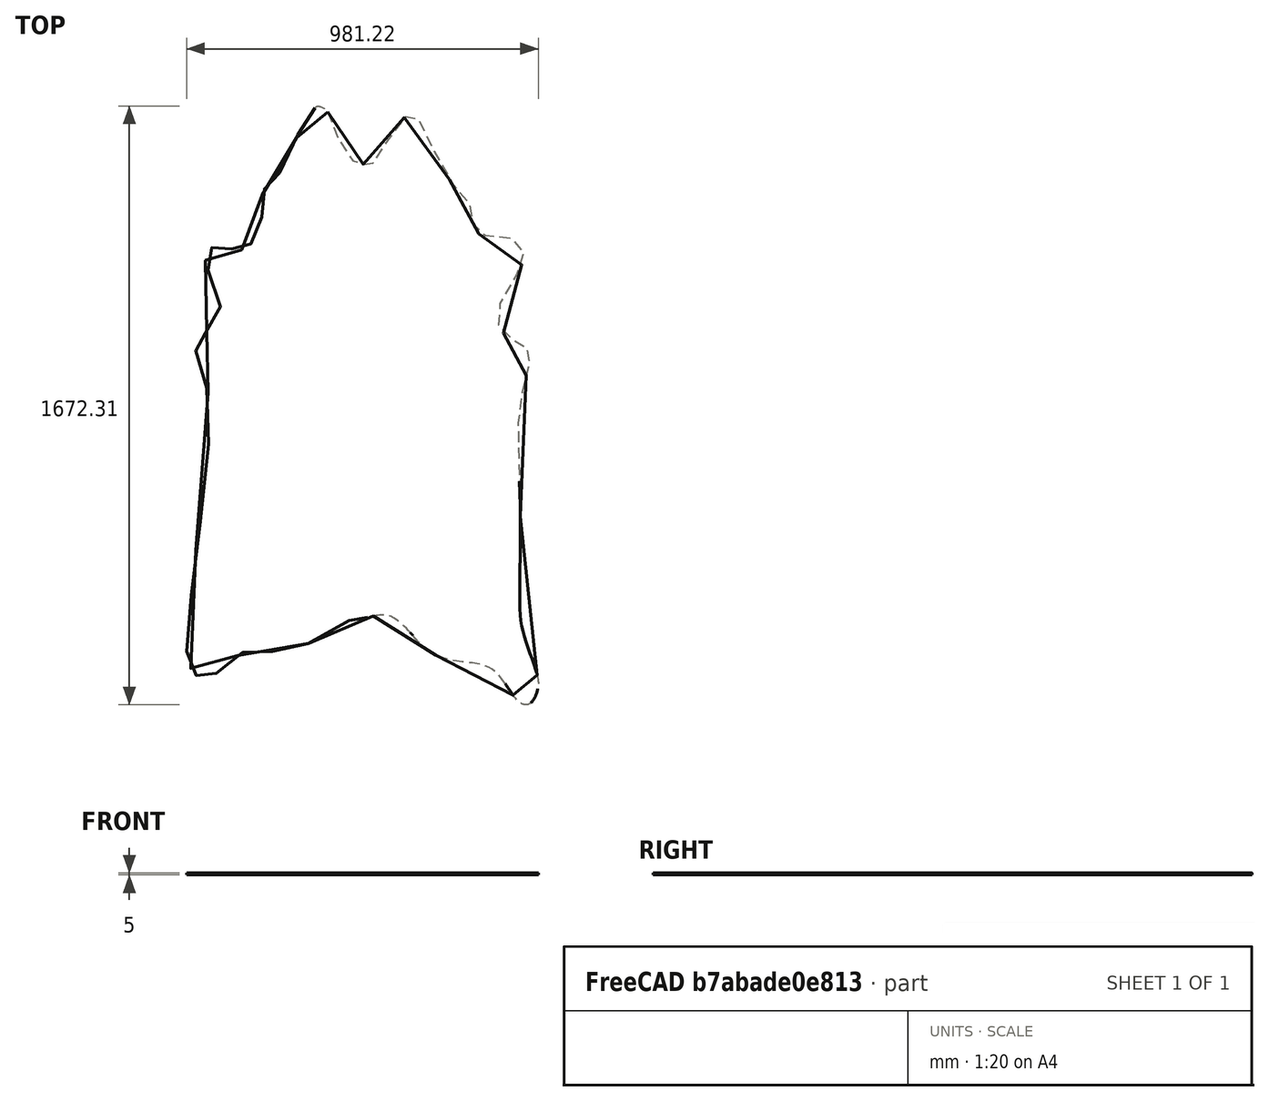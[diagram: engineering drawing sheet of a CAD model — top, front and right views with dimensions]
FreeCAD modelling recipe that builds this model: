
FCSTD DOCUMENT  (FreeCAD 0.21R33668 +26 (Git))
Label: Carpete de couro de vaca
License: All rights reserved
objects: Image::ImagePlane×2, Sketcher::SketchObject×1, Part::Extrusion×1, App::DocumentObjectGroup×1
note: 2 computed .brp shape members not serialized (recipe doc carries the construction recipe); baked Part::Feature solids carry a one-line shape summary decoded from their .brp

FEATURE [Image::ImagePlane] couro_vaca001  label="couro vaca001"
  XSize = 1300
  YSize = 1800
FEATURE [Sketcher::SketchObject] Sketch
  FullyConstrained = false
  sketch-geometry (228):
    g0-g112: Circle x113 (B-spline internal-alignment scaffolding for g113; pole/knot coordinates omitted)
    g113: BSplineCurve PolesCount=113 KnotsCount=114 Degree=3 IsPeriodic=1
    g114-g227: GeomPoint x114 (B-spline internal-alignment scaffolding for g113; pole/knot coordinates omitted)
  constraints (9):
    c: Weight(g0) = 1
    c: Equal(g0, g1-g6) x6
    c: PointOnObject(g6,g-2)
    c: Equal(g0, g7-g61) x55
    c: PointOnObject(g61,g-2)
    c: Equal(g0, g62-g112) x51
    c: PointOnObject(g112,g0)
    c: InternalAlignment(g0-g112 -> g113) x113
    c: InternalAlignment(g114-g227 -> g113) x114
FEATURE [Part::Extrusion] Extrude
  Base = -> Sketch
  Dir = (0,0,1)
  DirMode = 2
  FaceMakerClass = Part::FaceMakerBullseye
  LengthFwd = 5
  LengthRev = 0
  Solid = true
  Symmetric = false
FEATURE [Image::ImagePlane] couro_vaca002  label="couro vaca002"
  Placement = pos=(0,0,5) rot=(0,0,1;0rad)
  XSize = 1300
  YSize = 1800
FEATURE [App::DocumentObjectGroup] Group  label="Carpete"
  Group = -> [couro_vaca002,Extrude,couro_vaca001]
